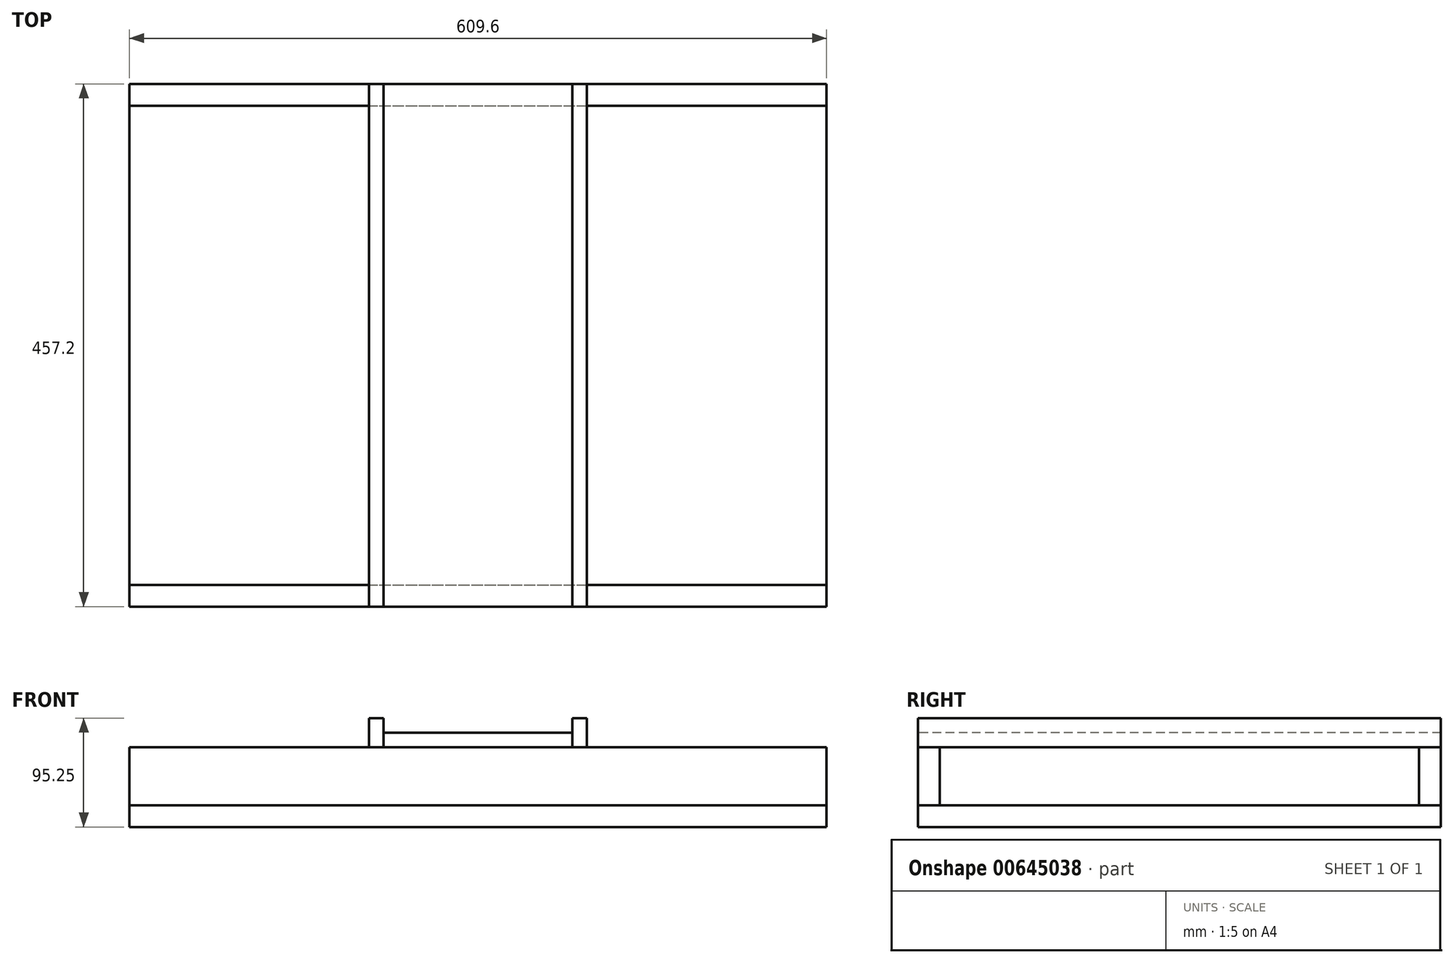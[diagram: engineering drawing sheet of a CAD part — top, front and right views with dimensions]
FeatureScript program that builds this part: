
annotation { "Feature Type Name" : "Feature", "Feature Type Description" : "" }
export const myFeature = defineFeature(function(context is Context, id is Id, definition is map)
    precondition{}
    {
        {
            var Q0;
            Q0=qCreatedBy(makeId("Top.planeOp"),FACE);
            var sketch = newSketch(context, id + "F0", { "sketchPlane" : qUnion([Q0])});
            skLineSegment(sketch, "E0.bottom", {"start": v(304.8, 228.6) * mm, "end": v(-304.8, 228.6) * mm});
            skLineSegment(sketch, "E0.top", {"start": v(304.8, -228.6) * mm, "end": v(-304.8, -228.6) * mm});
            skLineSegment(sketch, "E0.left", {"start": v(304.8, 228.6) * mm, "end": v(304.8, -228.6) * mm});
            skLineSegment(sketch, "E0.right", {"start": v(-304.8, 228.6) * mm, "end": v(-304.8, -228.6) * mm});
            skPoint(sketch, "E0.middle", {"position": v(0, 0) * mm});
            skSolve(sketch);
        }
        {
            var Q0;
            Q0 = qSketchRegion(id + "F0", true);
            extrude(context, id + "F1", {"entities" : qUnion([Q0]), "depth" : 19.05 * mm, "offsetDistance" : 25.4 * mm});
        }
        {
            var Q0;
            Q0=makeQuery(id+"F1.opExtrude","CAP_FACE",FACE,{"disambiguationData":[OSD([sQuery(id+"F0.wireOp",EDGE,"E0.bottom"),sQuery(id+"F0.wireOp",EDGE,"E0.top"),sQuery(id+"F0.wireOp",EDGE,"E0.left"),sQuery(id+"F0.wireOp",EDGE,"E0.right")])],"isStart":false});
            var sketch = newSketch(context, id + "F2", { "sketchPlane" : qUnion([Q0])});
            skLineSegment(sketch, "E1.bottom", {"start": v(-304.8, 228.6) * mm, "end": v(304.8, 228.6) * mm});
            skLineSegment(sketch, "E1.top", {"start": v(-304.8, 209.55) * mm, "end": v(304.8, 209.55) * mm});
            skLineSegment(sketch, "E1.left", {"start": v(-304.8, 228.6) * mm, "end": v(-304.8, 209.55) * mm});
            skLineSegment(sketch, "E1.right", {"start": v(304.8, 228.6) * mm, "end": v(304.8, 209.55) * mm});
            skLineSegment(sketch, "E2.bottom", {"start": v(-304.8, -228.6) * mm, "end": v(304.8, -228.6) * mm});
            skLineSegment(sketch, "E2.top", {"start": v(-304.8, -209.55) * mm, "end": v(304.8, -209.55) * mm});
            skLineSegment(sketch, "E2.left", {"start": v(-304.8, -228.6) * mm, "end": v(-304.8, -209.55) * mm});
            skLineSegment(sketch, "E2.right", {"start": v(304.8, -228.6) * mm, "end": v(304.8, -209.55) * mm});
            skSolve(sketch);
        }
        {
            var Q0;
            Q0 = qSketchRegion(id + "F2", true);
            extrude(context, id + "F3", {"entities" : qUnion([Q0]), "depth" : 50.8 * mm, "offsetDistance" : 25.4 * mm});
        }
        {
            var Q0;
            Q0=makeQuery(id+"F3.opExtrude","CAP_FACE",FACE,{"disambiguationData":[OSD([sQuery(id+"F2.wireOp",EDGE,"E2.bottom"),sQuery(id+"F2.wireOp",EDGE,"E2.top"),sQuery(id+"F2.wireOp",EDGE,"E2.left"),sQuery(id+"F2.wireOp",EDGE,"E2.right")])],"isStart":false});
            var sketch = newSketch(context, id + "F4", { "sketchPlane" : qUnion([Q0])});
            skPoint(sketch, "E3.0", {"position": v(0, 228.6) * mm});
            skLineSegment(sketch, "E4.0", {"start": v(304.8, 228.6) * mm, "end": v(-304.8, 228.6) * mm});
            skLineSegment(sketch, "E5.0", {"start": v(304.8, -228.6) * mm, "end": v(-304.8, -228.6) * mm});
            skLineSegment(sketch, "E6.bottom", {"start": v(82.55, 228.6) * mm, "end": v(-82.55, 228.6) * mm});
            skLineSegment(sketch, "E6.top", {"start": v(82.55, -228.6) * mm, "end": v(-82.55, -228.6) * mm});
            skLineSegment(sketch, "E6.left", {"start": v(82.55, 228.6) * mm, "end": v(82.55, -228.6) * mm});
            skLineSegment(sketch, "E6.right", {"start": v(-82.55, 228.6) * mm, "end": v(-82.55, -228.6) * mm});
            skPoint(sketch, "E6.middle", {"position": v(0, 0) * mm});
            skSolve(sketch);
        }
        {
            var Q0;
            Q0 = qSketchRegion(id + "F4", true);
            extrude(context, id + "F5", {"entities" : qUnion([Q0]), "depth" : 12.7 * mm, "offsetDistance" : 25.4 * mm});
        }
        {
            var Q0;
            Q0=makeQuery(id+"F3.opExtrude","CAP_FACE",FACE,{"disambiguationData":[OSD([sQuery(id+"F2.wireOp",EDGE,"E1.bottom"),sQuery(id+"F2.wireOp",EDGE,"E1.top"),sQuery(id+"F2.wireOp",EDGE,"E1.left"),sQuery(id+"F2.wireOp",EDGE,"E1.right")])],"isStart":false});
            var sketch = newSketch(context, id + "F6", { "sketchPlane" : qUnion([Q0])});
            skPoint(sketch, "E7.0", {"position": v(82.55, 228.6) * mm});
            skPoint(sketch, "E8.0", {"position": v(82.55, -228.6) * mm});
            skLineSegment(sketch, "E9.0", {"start": v(304.8, -228.6) * mm, "end": v(-304.8, -228.6) * mm});
            skPoint(sketch, "E10.0", {"position": v(-82.55, 228.6) * mm});
            skLineSegment(sketch, "E11.bottom", {"start": v(-82.55, 228.6) * mm, "end": v(-95.25, 228.6) * mm});
            skLineSegment(sketch, "E11.top", {"start": v(-82.55, -228.6) * mm, "end": v(-95.25, -228.6) * mm});
            skLineSegment(sketch, "E11.left", {"start": v(-82.55, 228.6) * mm, "end": v(-82.55, -228.6) * mm});
            skLineSegment(sketch, "E11.right", {"start": v(-95.25, 228.6) * mm, "end": v(-95.25, -228.6) * mm});
            skLineSegment(sketch, "E12.bottom", {"start": v(82.55, 228.6) * mm, "end": v(95.25, 228.6) * mm});
            skLineSegment(sketch, "E12.top", {"start": v(82.55, -228.6) * mm, "end": v(95.25, -228.6) * mm});
            skLineSegment(sketch, "E12.left", {"start": v(82.55, 228.6) * mm, "end": v(82.55, -228.6) * mm});
            skLineSegment(sketch, "E12.right", {"start": v(95.25, 228.6) * mm, "end": v(95.25, -228.6) * mm});
            skSolve(sketch);
        }
        {
            var Q0;
            Q0 = qSketchRegion(id + "F6", true);
            extrude(context, id + "F7", {"entities" : qUnion([Q0]), "depth" : 25.4 * mm, "offsetDistance" : 25.4 * mm});
        }
    });
